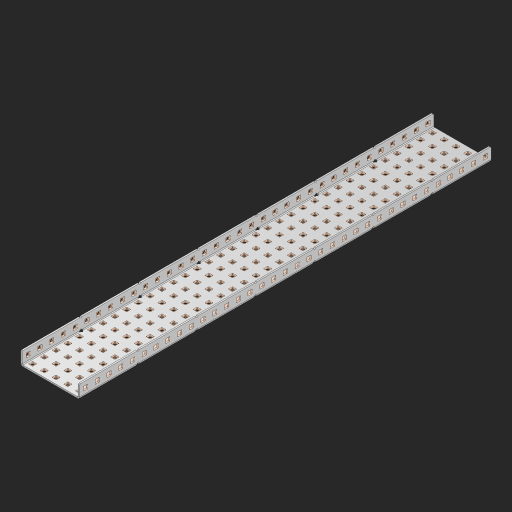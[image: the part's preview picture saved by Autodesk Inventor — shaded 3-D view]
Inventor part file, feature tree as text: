
AUTODESK INVENTOR PART (.ipt)
format: ipt  version: 2023 (Build 270158000, 158)  size: 2,542,080 bytes
history: native  units: in
note: dims shown in document units (in); Inventor stores cm internally (conversion verified against a paired STEP export)
features: other x496, extrude x244, sheet_metal_op x10, sketch x8, mirror x1, pattern_linear x1, chamfer x1
ambient origin geometry x8: Origin, YZ Plane, XZ Plane, XY Plane, X Axis, Y Axis, Z Axis, Center Point
bodies: Solid1 (feature_tree), Body (feature_tree)
feature tree (761):
  other  "Table"
  other  "Alu C 1x3x1x35"
  other  "Alu C 1x3x1x34"
  other  "Alu C 1x3x1x33"
  other  "Alu C 1x3x1x32"
  other  "Alu C 1x3x1x31"
  other  "Alu C 1x3x1x30"
  other  "Alu C 1x3x1x29"
  other  "Alu C 1x3x1x28"
  other  "Alu C 1x3x1x27"
  other  "Alu C 1x3x1x26"
  other  "Alu C 1x3x1x25"
  other  "Alu C 1x3x1x24"
  other  "Alu C 1x3x1x23"
  other  "Alu C 1x3x1x22"
  other  "Alu C 1x3x1x21"
  other  "Alu C 1x3x1x20"
  other  "Alu C 1x3x1x19"
  other  "Alu C 1x3x1x18"
  other  "Alu C 1x3x1x17"
  other  "Alu C 1x3x1x16"
  other  "Alu C 1x3x1x15"
  other  "Alu C 1x3x1x14"
  other  "Alu C 1x3x1x13"
  other  "Alu C 1x3x1x12"
  other  "Alu C 1x3x1x11"
  other  "Alu C 1x3x1x10"
  other  "Alu C 1x3x1x9"
  other  "Alu C 1x3x1x8"
  other  "Alu C 1x3x1x7"
  other  "Alu C 1x3x1x6"
  other  "Alu C 1x3x1x5"
  other  "Alu C 1x3x1x4"
  other  "Alu C 1x3x1x3"
  other  "Alu C 1x3x1x2"
  other  "Alu C 1x3x1x1"
  other  "Alu Half C 1x3x1x35"
  other  "Alu Half C 1x3x1x34"
  other  "Alu Half C 1x3x1x33"
  other  "Alu Half C 1x3x1x32"
  other  "Alu Half C 1x3x1x31"
  other  "Alu Half C 1x3x1x30"
  other  "Alu Half C 1x3x1x29"
  other  "Alu Half C 1x3x1x28"
  other  "Alu Half C 1x3x1x27"
  other  "Alu Half C 1x3x1x26"
  other  "Alu Half C 1x3x1x25"
  other  "Alu Half C 1x3x1x24"
  other  "Alu Half C 1x3x1x23"
  other  "Alu Half C 1x3x1x22"
  other  "Alu Half C 1x3x1x21"
  other  "Alu Half C 1x3x1x20"
  other  "Alu Half C 1x3x1x19"
  other  "Alu Half C 1x3x1x18"
  other  "Alu Half C 1x3x1x17"
  other  "Alu Half C 1x3x1x16"
  other  "Alu Half C 1x3x1x15"
  other  "Alu Half C 1x3x1x14"
  other  "Alu Half C 1x3x1x13"
  other  "Alu Half C 1x3x1x12"
  other  "Alu Half C 1x3x1x11"
  other  "Alu Half C 1x3x1x10"
  other  "Alu Half C 1x3x1x9"
  other  "Alu Half C 1x3x1x8"
  other  "Alu Half C 1x3x1x7"
  other  "Alu Half C 1x3x1x6"
  other  "Alu Half C 1x3x1x5"
  other  "Alu Half C 1x3x1x4"
  other  "Alu Half C 1x3x1x3"
  other  "Alu Half C 1x3x1x2"
  other  "Alu Half C 1x3x1x1"
  other  "Alu Half C Thick 1x3x1x35"
  other  "Alu Half C Thick 1x3x1x34"
  other  "Alu Half C Thick 1x3x1x33"
  other  "Alu Half C Thick 1x3x1x32"
  other  "Alu Half C Thick 1x3x1x31"
  other  "Alu Half C Thick 1x3x1x30"
  other  "Alu Half C Thick 1x3x1x29"
  other  "Alu Half C Thick 1x3x1x28"
  other  "Alu Half C Thick 1x3x1x27"
  other  "Alu Half C Thick 1x3x1x26"
  other  "Alu Half C Thick 1x3x1x25"
  other  "Alu Half C Thick 1x3x1x24"
  other  "Alu Half C Thick 1x3x1x23"
  other  "Alu Half C Thick 1x3x1x22"
  other  "Alu Half C Thick 1x3x1x21"
  other  "Alu Half C Thick 1x3x1x20"
  other  "Alu Half C Thick 1x3x1x19"
  other  "Alu Half C Thick 1x3x1x18"
  other  "Alu Half C Thick 1x3x1x17"
  other  "Alu Half C Thick 1x3x1x16"
  other  "Alu Half C Thick 1x3x1x15"
  other  "Alu Half C Thick 1x3x1x14"
  other  "Alu Half C Thick 1x3x1x13"
  other  "Alu Half C Thick 1x3x1x12"
  other  "Alu Half C Thick 1x3x1x11"
  other  "Alu Half C Thick 1x3x1x10"
  other  "Alu Half C Thick 1x3x1x9"
  other  "Alu Half C Thick 1x3x1x8"
  other  "Alu Half C Thick 1x3x1x7"
  other  "Alu Half C Thick 1x3x1x6"
  other  "Alu Half C Thick 1x3x1x5"
  other  "Alu Half C Thick 1x3x1x4"
  other  "Alu Half C Thick 1x3x1x3"
  other  "Alu Half C Thick 1x3x1x2"
  other  "Alu Half C Thick 1x3x1x1"
  other  "Alu C 1x5x1x35"
  other  "Alu C 1x5x1x34"
  other  "Alu C 1x5x1x33"
  other  "Alu C 1x5x1x32"
  other  "Alu C 1x5x1x31"
  other  "Alu C 1x5x1x30"
  other  "Alu C 1x5x1x29"
  other  "Alu C 1x5x1x28"
  other  "Alu C 1x5x1x27"
  other  "Alu C 1x5x1x26"
  other  "Alu C 1x5x1x25"
  other  "Alu C 1x5x1x24"
  other  "Alu C 1x5x1x23"
  other  "Alu C 1x5x1x22"
  other  "Alu C 1x5x1x21"
  other  "Alu C 1x5x1x20"
  other  "Alu C 1x5x1x19"
  other  "Alu C 1x5x1x18"
  other  "Alu C 1x5x1x17"
  other  "Alu C 1x5x1x16"
  other  "Alu C 1x5x1x15"
  other  "Alu C 1x5x1x14"
  other  "Alu C 1x5x1x13"
  other  "Alu C 1x5x1x12"
  other  "Alu C 1x5x1x11"
  other  "Alu C 1x5x1x10"
  other  "Alu C 1x5x1x9"
  other  "Alu C 1x5x1x8"
  other  "Alu C 1x5x1x7"
  other  "Alu C 1x5x1x6"
  other  "Alu C 1x5x1x5"
  other  "Alu C 1x5x1x4"
  other  "Alu C 1x5x1x3"
  other  "Alu C 1x5x1x2"
  other  "Alu C 1x5x1x1"
  other  "Steel C 1x5x1x35"
  other  "Steel C 1x5x1x34"
  other  "Steel C 1x5x1x33"
  other  "Steel C 1x5x1x32"
  other  "Steel C 1x5x1x31"
  other  "Steel C 1x5x1x30"
  other  "Steel C 1x5x1x29"
  other  "Steel C 1x5x1x28"
  other  "Steel C 1x5x1x27"
  other  "Steel C 1x5x1x26"
  other  "Steel C 1x5x1x25"
  other  "Steel C 1x5x1x24"
  other  "Steel C 1x5x1x23"
  other  "Steel C 1x5x1x22"
  other  "Steel C 1x5x1x21"
  other  "Steel C 1x5x1x20"
  other  "Steel C 1x5x1x19"
  other  "Steel C 1x5x1x18"
  other  "Steel C 1x5x1x17"
  other  "Steel C 1x5x1x16"
  other  "Steel C 1x5x1x15"
  other  "Steel C 1x5x1x14"
  other  "Steel C 1x5x1x13"
  other  "Steel C 1x5x1x12"
  other  "Steel C 1x5x1x11"
  other  "Steel C 1x5x1x10"
  other  "Steel C 1x5x1x9"
  other  "Steel C 1x5x1x8"
  other  "Steel C 1x5x1x7"
  other  "Steel C 1x5x1x6"
  other  "Steel C 1x5x1x5"
  other  "Steel C 1x5x1x4"
  other  "Steel C 1x5x1x3"
  other  "Steel C 1x5x1x2"
  other  "Steel C 1x5x1x1"
  other  "Steel Half C 1x5x1x35"
  other  "Steel Half C 1x5x1x34"
  other  "Steel Half C 1x5x1x33"
  other  "Steel Half C 1x5x1x32"
  other  "Steel Half C 1x5x1x31"
  other  "Steel Half C 1x5x1x30"
  other  "Steel Half C 1x5x1x29"
  other  "Steel Half C 1x5x1x28"
  other  "Steel Half C 1x5x1x27"
  other  "Steel Half C 1x5x1x26"
  other  "Steel Half C 1x5x1x25"
  other  "Steel Half C 1x5x1x24"
  other  "Steel Half C 1x5x1x23"
  other  "Steel Half C 1x5x1x22"
  other  "Steel Half C 1x5x1x21"
  other  "Steel Half C 1x5x1x20"
  other  "Steel Half C 1x5x1x19"
  other  "Steel Half C 1x5x1x18"
  other  "Steel Half C 1x5x1x17"
  other  "Steel Half C 1x5x1x16"
  other  "Steel Half C 1x5x1x15"
  other  "Steel Half C 1x5x1x14"
  other  "Steel Half C 1x5x1x13"
  other  "Steel Half C 1x5x1x12"
  other  "Steel Half C 1x5x1x11"
  other  "Steel Half C 1x5x1x10"
  other  "Steel Half C 1x5x1x9"
  other  "Steel Half C 1x5x1x8"
  other  "Steel Half C 1x5x1x7"
  other  "Steel Half C 1x5x1x6"
  other  "Steel Half C 1x5x1x5"
  other  "Steel Half C 1x5x1x4"
  other  "Steel Half C 1x5x1x3"
  other  "Steel Half C 1x5x1x2"
  other  "Steel Half C 1x5x1x1"
  other  "Steel Half C Thick 1x5x1x35"
  other  "Steel Half C Thick 1x5x1x34"
  other  "Steel Half C Thick 1x5x1x33"
  other  "Steel Half C Thick 1x5x1x32"
  other  "Steel Half C Thick 1x5x1x31"
  other  "Steel Half C Thick 1x5x1x30"
  other  "Steel Half C Thick 1x5x1x29"
  other  "Steel Half C Thick 1x5x1x28"
  other  "Steel Half C Thick 1x5x1x27"
  other  "Steel Half C Thick 1x5x1x26"
  other  "Steel Half C Thick 1x5x1x25"
  other  "Steel Half C Thick 1x5x1x24"
  other  "Steel Half C Thick 1x5x1x23"
  other  "Steel Half C Thick 1x5x1x22"
  other  "Steel Half C Thick 1x5x1x21"
  other  "Steel Half C Thick 1x5x1x20"
  other  "Steel Half C Thick 1x5x1x19"
  other  "Steel Half C Thick 1x5x1x18"
  other  "Steel Half C Thick 1x5x1x17"
  other  "Steel Half C Thick 1x5x1x16"
  other  "Steel Half C Thick 1x5x1x15"
  other  "Steel Half C Thick 1x5x1x14"
  other  "Steel Half C Thick 1x5x1x13"
  other  "Steel Half C Thick 1x5x1x12"
  other  "Steel Half C Thick 1x5x1x11"
  other  "Steel Half C Thick 1x5x1x10"
  other  "Steel Half C Thick 1x5x1x9"
  other  "Steel Half C Thick 1x5x1x8"
  other  "Steel Half C Thick 1x5x1x7"
  other  "Steel Half C Thick 1x5x1x6"
  other  "Steel Half C Thick 1x5x1x5"
  other  "Steel Half C Thick 1x5x1x4"
  other  "Steel Half C Thick 1x5x1x3"
  other  "Steel Half C Thick 1x5x1x2"
  other  "Steel Half C Thick 1x5x1x1"
  other  "Flange Pattern Plane"
  sheet_metal_op  "Flange Pattern"
  sheet_metal_op  "Body Pattern"
  other  "Arc Length"
  mirror  "Notch Mirror"
  pattern_linear  "Notch Pattern"  Spacing1=0.25in  [1 undecoded]
  chamfer  "End Chamfer"
  extrude  "Half Cut"  Depth=0.0625in
  sketch  "Sketch1"  dims[d0=2.5in]
  other  "Plate1"
  sketch  "Sketch2"  dims[d1=17.5in]
  other  "Plate2"
  sheet_metal_op  "Bend1"
  sheet_metal_op  "Corner1"
  sketch  "Sketch3"  dims[d2=0.0625in]
  other  "Flange Pattern Sketch"
  sketch  "Sketch7"  dims[d3=0.0625in]
  other  "Srf1"
  other  "Srf2"
  sketch  "Sketch8"  dims[d4=0.0312in]
  sketch  "Sketch9"  dims[d5=0.125in]
  other  "Srf91"
  sheet_metal_op  "Body Pattern Sketch"
  other  "Srf92"
  sketch  "Sketch13"  dims[d6=0.0625in]
  sketch  "Sketch14"  dims[d7=0.5in d8=90.0deg d9=0.0312in d10=0.25in d11=0.0625in d12=0.0625in d16=0.182in d17=0.02in d18=0.0625in d19=0.0in d20=0.25in d21=0.25in d46=0.172in d47=1.0in d48=0.0in d49=0.182in d50=0.02in d51=0.25in d52=0.25in d53=0.0625in d54=0.0in d55=0.172in d56=1.0in d57=0.0in d60=13.7795in d62=0.5in d63=1.9685in d65=0.5in d85=0.1473in d86=0.1782in d88=0.04in d89=0.0625in d90=0.0in d91=0.04in d92=0.0491in d95=2.5in d96=0.04in d97=0.25in d98=45.0deg d101=0.0in d102=2.497in d131=2.5in d132=13.7795in d134=0.5in d139=0.5in]
  other  "Srf856"
  other  "Srf1310"
  other  "Srf1311"
  other  "Srf1312"
  other  "Srf1376"
  other  "Srf1377"
  other  "Srf1728"
  other  "Srf1755"
  other  "Srf1878"
  other  "Srf1879"
  other  "Srf1880"
  other  "Srf1881"
  other  "Srf1882"
  other  "Srf1883"
  other  "Srf1884"
  other  "Srf1885"
  other  "Srf1886"
  other  "Srf1887"
  other  "Srf1888"
  other  "Srf1889"
  other  "Srf1890"
  other  "Srf1891"
  other  "Srf1892"
  other  "Srf1893"
  other  "Srf1894"
  other  "Srf1895"
  other  "Srf1896"
  other  "Srf1897"
  other  "Srf1898"
  other  "Srf1899"
  other  "Srf1900"
  other  "Srf1901"
  other  "Srf1902"
  other  "Srf1903"
  other  "Srf1904"
  other  "Srf1905"
  other  "Srf1906"
  other  "Srf1942"
  other  "Srf1943"
  other  "Srf1944"
  other  "Srf1945"
  other  "Srf1946"
  other  "Srf1947"
  other  "Srf1948"
  other  "Srf1949"
  other  "Srf1950"
  other  "Srf1951"
  other  "Srf1952"
  other  "Srf1953"
  other  "Srf1954"
  other  "Srf1955"
  other  "Srf1956"
  other  "Srf1957"
  other  "Srf1958"
  other  "Srf1959"
  other  "Srf1960"
  other  "Srf1961"
  other  "Srf1962"
  other  "Srf1963"
  other  "Srf1964"
  other  "Srf1965"
  other  "Srf1966"
  other  "Srf1967"
  other  "Srf1968"
  other  "Srf1969"
  other  "Srf1970"
  other  "Srf2111"
  other  "Srf2112"
  other  "Srf2113"
  other  "Srf2114"
  other  "Srf2115"
  other  "Srf2116"
  other  "Srf2117"
  other  "Srf2118"
  other  "Srf2119"
  other  "Srf2120"
  other  "Srf2121"
  other  "Srf2122"
  other  "Srf2123"
  other  "Srf2124"
  other  "Srf2125"
  other  "Srf2126"
  other  "Srf2127"
  other  "Srf2128"
  other  "Srf2129"
  other  "Srf2130"
  other  "Srf2131"
  other  "Srf2132"
  other  "Srf2133"
  other  "Srf2134"
  other  "Srf2135"
  other  "Srf2136"
  other  "Srf2137"
  other  "Srf2138"
  other  "Srf2139"
  other  "Srf2140"
  other  "Srf2141"
  other  "Srf2142"
  other  "Srf2143"
  other  "Srf2144"
  other  "Srf2145"
  other  "Srf2146"
  other  "Srf2147"
  other  "Srf2148"
  other  "Srf2149"
  other  "Srf2150"
  other  "Srf2151"
  other  "Srf2152"
  other  "Srf2153"
  other  "Srf2154"
  other  "Srf2155"
  other  "Srf2156"
  other  "Srf2157"
  other  "Srf2158"
  other  "Srf2159"
  other  "Srf2160"
  other  "Srf2161"
  other  "Srf2162"
  other  "Srf2163"
  other  "Srf2164"
  other  "Srf2165"
  other  "Srf2166"
  other  "Srf2167"
  other  "Srf2168"
  other  "Srf2169"
  other  "Srf2170"
  other  "Srf2171"
  other  "Srf2172"
  other  "Srf2173"
  other  "Srf2174"
  other  "Srf2175"
  other  "Srf2176"
  other  "Srf2177"
  other  "Srf2178"
  other  "Srf2179"
  other  "Srf2180"
  other  "Srf2181"
  other  "Srf2182"
  other  "Srf2183"
  other  "Srf2184"
  other  "Srf2185"
  other  "Srf2186"
  other  "Srf2187"
  other  "Srf2188"
  other  "Srf2189"
  other  "Srf2190"
  other  "Srf2191"
  other  "Srf2192"
  other  "Srf2193"
  other  "Srf2194"
  other  "Srf2195"
  other  "Srf2196"
  other  "Srf2197"
  other  "Srf2198"
  other  "Srf2199"
  other  "Srf2200"
  other  "Srf2201"
  other  "Srf2202"
  other  "Srf2203"
  other  "Srf2204"
  other  "Srf2205"
  other  "Srf2206"
  other  "Srf2207"
  other  "Srf2208"
  other  "Srf2209"
  other  "Srf2210"
  other  "Srf2211"
  other  "Srf2212"
  other  "Srf2213"
  other  "Srf2214"
  other  "Srf2215"
  other  "Srf2216"
  other  "Srf2217"
  other  "Srf2218"
  other  "Srf2219"
  other  "Srf2220"
  other  "Srf2221"
  other  "Srf2222"
  other  "Srf2223"
  other  "Srf2224"
  other  "Srf2225"
  other  "Srf2226"
  other  "Srf2227"
  other  "Srf2228"
  other  "Srf2229"
  other  "Srf2230"
  other  "Srf2231"
  other  "Srf2232"
  other  "Srf2233"
  other  "Srf2234"
  other  "Srf2235"
  other  "Srf2236"
  other  "Srf2237"
  other  "Srf2238"
  other  "Srf2239"
  other  "Srf2240"
  other  "Srf2241"
  other  "Srf2242"
  other  "Srf2243"
  other  "Srf2244"
  other  "Srf2245"
  other  "Srf2246"
  other  "Srf2247"
  other  "Srf2248"
  other  "Srf2249"
  other  "Srf2250"
  other  "Srf2251"
  other  "Srf2252"
  other  "Srf2253"
  other  "Srf2254"
  other  "Srf2255"
  other  "Srf2256"
  other  "Srf2257"
  other  "Srf2258"
  other  "Srf2259"
  other  "Srf2260"
  other  "Srf2261"
  other  "Srf2262"
  other  "Srf2263"
  other  "Srf2264"
  other  "Srf2265"
  other  "Srf2266"
  other  "Srf2267"
  other  "Srf2268"
  other  "Srf2269"
  other  "Srf2270"
  other  "Srf2271"
  other  "Srf2272"
  other  "Srf2273"
  other  "Srf2274"
  other  "Srf2275"
  other  "Srf2276"
  other  "Srf2277"
  other  "Srf2278"
  other  "Srf2279"
  other  "Srf2280"
  other  "Srf2281"
  other  "Srf2282"
  other  "Srf2283"
  other  "Srf2284"
  other  "Srf2285"
  sheet_metal_op  "Flange Stamp"
  sheet_metal_op  "Flange Circle"
  sheet_metal_op  "Body Stamp"
  sheet_metal_op  "Body Circle"
  sheet_metal_op  "Notch"
  extrude  "ExtrusionSrf2"  Depth=0.0625in
  extrude  "ExtrusionSrf92"  Depth=2.5in
  extrude  "ExtrusionSrf856"  Depth=0.02in
  extrude  "ExtrusionSrf1310"  Depth=0.0625in
  extrude  "ExtrusionSrf1311"  TaperAngle=0.0deg  [1 undecoded]
  extrude  "ExtrusionSrf1312"  Depth=0.25in
  extrude  "ExtrusionSrf1376"  Depth=0.25in
  extrude  "ExtrusionSrf1377"  Depth=2.5in
  extrude  "ExtrusionSrf1728"  Depth=2.5in TaperAngle=0.0deg
  extrude  "ExtrusionSrf1755"  Depth=2.5in
  extrude  "ExtrusionSrf1878"  Depth=0.02in
  extrude  "ExtrusionSrf1879"  Depth=0.25in
  extrude  "ExtrusionSrf1880"  Depth=0.25in
  extrude  "ExtrusionSrf1881"  Depth=0.0625in
  extrude  "ExtrusionSrf1882"  TaperAngle=0.0deg  [1 undecoded]
  extrude  "ExtrusionSrf1883"  Depth=2.5in
  extrude  "ExtrusionSrf1884"  Depth=2.5in TaperAngle=0.0deg
  extrude  "ExtrusionSrf1885"  Depth=2.5in
  extrude  "ExtrusionSrf1886"  Depth=2.5in
  extrude  "ExtrusionSrf1887"  Depth=2.5in
  extrude  "ExtrusionSrf1888"  Depth=2.5in
  extrude  "ExtrusionSrf1889"  Depth=2.5in
  extrude  "ExtrusionSrf1890"  Depth=0.0625in
  extrude  "ExtrusionSrf1891"  TaperAngle=0.0deg  [1 undecoded]
  extrude  "ExtrusionSrf1892"  Depth=2.5in
  extrude  "ExtrusionSrf1893"  Depth=2.5in
  extrude  "ExtrusionSrf1894"  Depth=2.5in
  extrude  "ExtrusionSrf1895"  Depth=0.25in TaperAngle=45.0deg
  extrude  "ExtrusionSrf1896"  TaperAngle=0.0deg  [1 undecoded]
  extrude  "ExtrusionSrf1897"  Depth=2.5in
  extrude  "ExtrusionSrf1898"  Depth=2.5in
  extrude  "ExtrusionSrf1899"  Depth=2.5in
  extrude  "ExtrusionSrf1900"  Depth=2.5in
  extrude  "ExtrusionSrf1901"  Depth=2.5in
  extrude  "ExtrusionSrf1902"  [1 undecoded]
  extrude  "ExtrusionSrf1903"  [1 undecoded]
  extrude  "ExtrusionSrf1904"  [1 undecoded]
  extrude  "ExtrusionSrf1905"  [1 undecoded]
  extrude  "ExtrusionSrf1906"  [1 undecoded]
  extrude  "ExtrusionSrf1942"  [1 undecoded]
  extrude  "ExtrusionSrf1943"  [1 undecoded]
  extrude  "ExtrusionSrf1944"  [1 undecoded]
  extrude  "ExtrusionSrf1945"  [1 undecoded]
  extrude  "ExtrusionSrf1946"  [1 undecoded]
  extrude  "ExtrusionSrf1947"  [1 undecoded]
  extrude  "ExtrusionSrf1948"  [1 undecoded]
  extrude  "ExtrusionSrf1949"  [1 undecoded]
  extrude  "ExtrusionSrf1950"  [1 undecoded]
  extrude  "ExtrusionSrf1951"  [1 undecoded]
  extrude  "ExtrusionSrf1952"  [1 undecoded]
  extrude  "ExtrusionSrf1953"  [1 undecoded]
  extrude  "ExtrusionSrf1954"  [1 undecoded]
  extrude  "ExtrusionSrf1955"  [1 undecoded]
  extrude  "ExtrusionSrf1956"  [1 undecoded]
  extrude  "ExtrusionSrf1957"  [1 undecoded]
  extrude  "ExtrusionSrf1958"  [1 undecoded]
  extrude  "ExtrusionSrf1959"  [1 undecoded]
  extrude  "ExtrusionSrf1960"  [1 undecoded]
  extrude  "ExtrusionSrf1961"  [1 undecoded]
  extrude  "ExtrusionSrf1962"  [1 undecoded]
  extrude  "ExtrusionSrf1963"  [1 undecoded]
  extrude  "ExtrusionSrf1964"  [1 undecoded]
  extrude  "ExtrusionSrf1965"  [1 undecoded]
  extrude  "ExtrusionSrf1966"  [1 undecoded]
  extrude  "ExtrusionSrf1967"  [1 undecoded]
  extrude  "ExtrusionSrf1968"  [1 undecoded]
  extrude  "ExtrusionSrf1969"  [1 undecoded]
  extrude  "ExtrusionSrf1970"  [1 undecoded]
  extrude  "ExtrusionSrf2111"  [1 undecoded]
  extrude  "ExtrusionSrf2112"  [1 undecoded]
  extrude  "ExtrusionSrf2113"  [1 undecoded]
  extrude  "ExtrusionSrf2114"  [1 undecoded]
  extrude  "ExtrusionSrf2115"  [1 undecoded]
  extrude  "ExtrusionSrf2116"  [1 undecoded]
  extrude  "ExtrusionSrf2117"  [1 undecoded]
  extrude  "ExtrusionSrf2118"  [1 undecoded]
  extrude  "ExtrusionSrf2119"  [1 undecoded]
  extrude  "ExtrusionSrf2120"  [1 undecoded]
  extrude  "ExtrusionSrf2121"  [1 undecoded]
  extrude  "ExtrusionSrf2122"  [1 undecoded]
  extrude  "ExtrusionSrf2123"  [1 undecoded]
  extrude  "ExtrusionSrf2124"  [1 undecoded]
  extrude  "ExtrusionSrf2125"  [1 undecoded]
  extrude  "ExtrusionSrf2126"  [1 undecoded]
  extrude  "ExtrusionSrf2127"  [1 undecoded]
  extrude  "ExtrusionSrf2128"  [1 undecoded]
  extrude  "ExtrusionSrf2129"  [1 undecoded]
  extrude  "ExtrusionSrf2130"  [1 undecoded]
  extrude  "ExtrusionSrf2131"  [1 undecoded]
  extrude  "ExtrusionSrf2132"  [1 undecoded]
  extrude  "ExtrusionSrf2133"  [1 undecoded]
  extrude  "ExtrusionSrf2134"  [1 undecoded]
  extrude  "ExtrusionSrf2135"  [1 undecoded]
  extrude  "ExtrusionSrf2136"  [1 undecoded]
  extrude  "ExtrusionSrf2137"  [1 undecoded]
  extrude  "ExtrusionSrf2138"  [1 undecoded]
  extrude  "ExtrusionSrf2139"  [1 undecoded]
  extrude  "ExtrusionSrf2140"  [1 undecoded]
  extrude  "ExtrusionSrf2141"  [1 undecoded]
  extrude  "ExtrusionSrf2142"  [1 undecoded]
  extrude  "ExtrusionSrf2143"  [1 undecoded]
  extrude  "ExtrusionSrf2144"  [1 undecoded]
  extrude  "ExtrusionSrf2145"  [1 undecoded]
  extrude  "ExtrusionSrf2146"  [1 undecoded]
  extrude  "ExtrusionSrf2147"  [1 undecoded]
  extrude  "ExtrusionSrf2148"  [1 undecoded]
  extrude  "ExtrusionSrf2149"  [1 undecoded]
  extrude  "ExtrusionSrf2150"  [1 undecoded]
  extrude  "ExtrusionSrf2151"  [1 undecoded]
  extrude  "ExtrusionSrf2152"  [1 undecoded]
  extrude  "ExtrusionSrf2153"  [1 undecoded]
  extrude  "ExtrusionSrf2154"  [1 undecoded]
  extrude  "ExtrusionSrf2155"  [1 undecoded]
  extrude  "ExtrusionSrf2156"  [1 undecoded]
  extrude  "ExtrusionSrf2157"  [1 undecoded]
  extrude  "ExtrusionSrf2158"  [1 undecoded]
  extrude  "ExtrusionSrf2159"  [1 undecoded]
  extrude  "ExtrusionSrf2160"  [1 undecoded]
  extrude  "ExtrusionSrf2161"  [1 undecoded]
  extrude  "ExtrusionSrf2162"  [1 undecoded]
  extrude  "ExtrusionSrf2163"  [1 undecoded]
  extrude  "ExtrusionSrf2164"  [1 undecoded]
  extrude  "ExtrusionSrf2165"  [1 undecoded]
  extrude  "ExtrusionSrf2166"  [1 undecoded]
  extrude  "ExtrusionSrf2167"  [1 undecoded]
  extrude  "ExtrusionSrf2168"  [1 undecoded]
  extrude  "ExtrusionSrf2169"  [1 undecoded]
  extrude  "ExtrusionSrf2170"  [1 undecoded]
  extrude  "ExtrusionSrf2171"  [1 undecoded]
  extrude  "ExtrusionSrf2172"  [1 undecoded]
  extrude  "ExtrusionSrf2173"  [1 undecoded]
  extrude  "ExtrusionSrf2174"  [1 undecoded]
  extrude  "ExtrusionSrf2175"  [1 undecoded]
  extrude  "ExtrusionSrf2176"  [1 undecoded]
  extrude  "ExtrusionSrf2177"  [1 undecoded]
  extrude  "ExtrusionSrf2178"  [1 undecoded]
  extrude  "ExtrusionSrf2179"  [1 undecoded]
  extrude  "ExtrusionSrf2180"  [1 undecoded]
  extrude  "ExtrusionSrf2181"  [1 undecoded]
  extrude  "ExtrusionSrf2182"  [1 undecoded]
  extrude  "ExtrusionSrf2183"  [1 undecoded]
  extrude  "ExtrusionSrf2184"  [1 undecoded]
  extrude  "ExtrusionSrf2185"  [1 undecoded]
  extrude  "ExtrusionSrf2186"  [1 undecoded]
  extrude  "ExtrusionSrf2187"  [1 undecoded]
  extrude  "ExtrusionSrf2188"  [1 undecoded]
  extrude  "ExtrusionSrf2189"  [1 undecoded]
  extrude  "ExtrusionSrf2190"  [1 undecoded]
  extrude  "ExtrusionSrf2191"  [1 undecoded]
  extrude  "ExtrusionSrf2192"  [1 undecoded]
  extrude  "ExtrusionSrf2193"  [1 undecoded]
  extrude  "ExtrusionSrf2194"  [1 undecoded]
  extrude  "ExtrusionSrf2195"  [1 undecoded]
  extrude  "ExtrusionSrf2196"  [1 undecoded]
  extrude  "ExtrusionSrf2197"  [1 undecoded]
  extrude  "ExtrusionSrf2198"  [1 undecoded]
  extrude  "ExtrusionSrf2199"  [1 undecoded]
  extrude  "ExtrusionSrf2200"  [1 undecoded]
  extrude  "ExtrusionSrf2201"  [1 undecoded]
  extrude  "ExtrusionSrf2202"  [1 undecoded]
  extrude  "ExtrusionSrf2203"  [1 undecoded]
  extrude  "ExtrusionSrf2204"  [1 undecoded]
  extrude  "ExtrusionSrf2205"  [1 undecoded]
  extrude  "ExtrusionSrf2206"  [1 undecoded]
  extrude  "ExtrusionSrf2207"  [1 undecoded]
  extrude  "ExtrusionSrf2208"  [1 undecoded]
  extrude  "ExtrusionSrf2209"  [1 undecoded]
  extrude  "ExtrusionSrf2210"  [1 undecoded]
  extrude  "ExtrusionSrf2211"  [1 undecoded]
  extrude  "ExtrusionSrf2212"  [1 undecoded]
  extrude  "ExtrusionSrf2213"  [1 undecoded]
  extrude  "ExtrusionSrf2214"  [1 undecoded]
  extrude  "ExtrusionSrf2215"  [1 undecoded]
  extrude  "ExtrusionSrf2216"  [1 undecoded]
  extrude  "ExtrusionSrf2217"  [1 undecoded]
  extrude  "ExtrusionSrf2218"  [1 undecoded]
  extrude  "ExtrusionSrf2219"  [1 undecoded]
  extrude  "ExtrusionSrf2220"  [1 undecoded]
  extrude  "ExtrusionSrf2221"  [1 undecoded]
  extrude  "ExtrusionSrf2222"  [1 undecoded]
  extrude  "ExtrusionSrf2223"  [1 undecoded]
  extrude  "ExtrusionSrf2224"  [1 undecoded]
  extrude  "ExtrusionSrf2225"  [1 undecoded]
  extrude  "ExtrusionSrf2226"  [1 undecoded]
  extrude  "ExtrusionSrf2227"  [1 undecoded]
  extrude  "ExtrusionSrf2228"  [1 undecoded]
  extrude  "ExtrusionSrf2229"  [1 undecoded]
  extrude  "ExtrusionSrf2230"  [1 undecoded]
  extrude  "ExtrusionSrf2231"  [1 undecoded]
  extrude  "ExtrusionSrf2232"  [1 undecoded]
  extrude  "ExtrusionSrf2233"  [1 undecoded]
  extrude  "ExtrusionSrf2234"  [1 undecoded]
  extrude  "ExtrusionSrf2235"  [1 undecoded]
  extrude  "ExtrusionSrf2236"  [1 undecoded]
  extrude  "ExtrusionSrf2237"  [1 undecoded]
  extrude  "ExtrusionSrf2238"  [1 undecoded]
  extrude  "ExtrusionSrf2239"  [1 undecoded]
  extrude  "ExtrusionSrf2240"  [1 undecoded]
  extrude  "ExtrusionSrf2241"  [1 undecoded]
  extrude  "ExtrusionSrf2242"  [1 undecoded]
  extrude  "ExtrusionSrf2243"  [1 undecoded]
  extrude  "ExtrusionSrf2244"  [1 undecoded]
  extrude  "ExtrusionSrf2245"  [1 undecoded]
  extrude  "ExtrusionSrf2246"  [1 undecoded]
  extrude  "ExtrusionSrf2247"  [1 undecoded]
  extrude  "ExtrusionSrf2248"  [1 undecoded]
  extrude  "ExtrusionSrf2249"  [1 undecoded]
  extrude  "ExtrusionSrf2250"  [1 undecoded]
  extrude  "ExtrusionSrf2251"  [1 undecoded]
  extrude  "ExtrusionSrf2252"  [1 undecoded]
  extrude  "ExtrusionSrf2253"  [1 undecoded]
  extrude  "ExtrusionSrf2254"  [1 undecoded]
  extrude  "ExtrusionSrf2255"  [1 undecoded]
  extrude  "ExtrusionSrf2256"  [1 undecoded]
  extrude  "ExtrusionSrf2257"  [1 undecoded]
  extrude  "ExtrusionSrf2258"  [1 undecoded]
  extrude  "ExtrusionSrf2259"  [1 undecoded]
  extrude  "ExtrusionSrf2260"  [1 undecoded]
  extrude  "ExtrusionSrf2261"  [1 undecoded]
  extrude  "ExtrusionSrf2262"  [1 undecoded]
  extrude  "ExtrusionSrf2263"  [1 undecoded]
  extrude  "ExtrusionSrf2264"  [1 undecoded]
  extrude  "ExtrusionSrf2265"  [1 undecoded]
  extrude  "ExtrusionSrf2266"  [1 undecoded]
  extrude  "ExtrusionSrf2267"  [1 undecoded]
  extrude  "ExtrusionSrf2268"  [1 undecoded]
  extrude  "ExtrusionSrf2269"  [1 undecoded]
  extrude  "ExtrusionSrf2270"  [1 undecoded]
  extrude  "ExtrusionSrf2271"  [1 undecoded]
  extrude  "ExtrusionSrf2272"  [1 undecoded]
  extrude  "ExtrusionSrf2273"  [1 undecoded]
  extrude  "ExtrusionSrf2274"  [1 undecoded]
  extrude  "ExtrusionSrf2275"  [1 undecoded]
  extrude  "ExtrusionSrf2276"  [1 undecoded]
  extrude  "ExtrusionSrf2277"  [1 undecoded]
  extrude  "ExtrusionSrf2278"  [1 undecoded]
  extrude  "ExtrusionSrf2279"  [1 undecoded]
  extrude  "ExtrusionSrf2280"  [1 undecoded]
  extrude  "ExtrusionSrf2281"  [1 undecoded]
  extrude  "ExtrusionSrf2282"  [1 undecoded]
  extrude  "ExtrusionSrf2283"  [1 undecoded]
  extrude  "ExtrusionSrf2284"  [1 undecoded]
  extrude  "ExtrusionSrf2285"  [1 undecoded]
note: 214 required parameter values undecoded (feature->parameter linkage not recoverable at this tier; creation-order binding heuristic only, values carry confidence <= 0.55)
